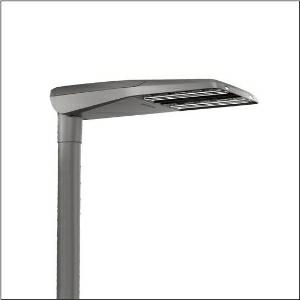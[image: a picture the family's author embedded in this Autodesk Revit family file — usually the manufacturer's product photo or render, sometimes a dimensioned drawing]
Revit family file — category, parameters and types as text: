
# Revit family: streetlight_sl_11_iq_midi___st0_5st0_5_5xc3h51f08me_c4bc
name_source: partatom
category: Lighting Fixtures
units: mm (PartAtom-declared; Revit-internal decimal feet)

## family parameters
Cut with Voids When Loaded = No
Host = Face
Light Source = No
Part Type = Normal
Room Calculation Point = No
Round Connector Dimension = Use Diameter
Shared = No

## types (1)
- --- (1 x LED, 17940 lm, 124.7 W, 3000K)
    Apparent Load = 125 VA
    CIE Flux Codes = 43 74 97 100 100
    Color Rendering = 70
    Color Temperature = 3000K
    Default Elevation = 1800 mm
    Description = Streetlight SL 11 iQ midi, mast luminaire, primary light control with 3 zone facetted reflector, of plastic, silver coated, highly specular, primary optical cover: cover, of PMMA, transparent, light distribution: ST0.5ST0.5, light emission: direct distribution, primary light characteristic: asymmetric, installation type: post-top, side-entry, LED, High Power LED, rated luminous flux: 17.940lm, luminous efficacy: 144lm/W, light colour: 730, colour temperature: 3000K, control: Street-Remote, optimised constant luminous flux control (CLO 2.0), Desk-Remote (wireless, voltage-free reading and setting of iQ features in the workshop via application-optimized NFC function/RFID function), Light-Fading, Smart-Wire, Night-Set, Lumen-Switch, Temp-Guard, Auto-Match, with cable H07RN-F 5x 1.5mm², mains connection: 220..240V, AC, 50/60Hz, connection cable pre-assembled, cable length: 12,5m, start of lifetime: 125W, end of lifetime: 132W, reduction: 57W, luminaire housing, of diecast aluminium, powder-coated, Siteco® metallic grey (DB 702S), length: 780mm, width: 376mm, height: 118mm, spigot size: 60/76mm (post-top) and 42/60/76mm (side-entry), mast flange for spigot size: 42mm: 5XC10008XM4, 60mm: 5XC10008XM2, 76/60mm: 5XC10108XM1, equipment: Power, protection rating (complete): IP66, insulation class (complete): insulation class II (safety insulation), certification: CE, ENEC, VDE, impact resistance: IK09, permissible operating ambient temperature for outdoor applications: -25..+50°C, standard-compliant lighting for roads and squares, packaging unit: 1 piece

Light Distribution: ST0.5ST0.5
    Height = 118 mm
    Lamp = 1 x LED
    Lamp Light Flux = 17940 lm
    Lamp Power = 124.7 W
    Lamp count = 1
    Length = 780 mm
    Luminous efficacy = 144 lm/W
    Manufacturer = Siteco
    ModVariant = No
    Model = 5XC3H51F08ME
    Number of Poles = 1
    OnlyDefault = Yes
    Power Factor = 1
    Product Name = Streetlight SL 11 iQ midi | ST0.5ST0.5
    Product group = mast luminaire | pylon top
    ProductGroupID = 6100
    Protection Class = Protection class II
    Protection Degree = IP 66
    RLX_Detail_Level = 1
    RlxData = <blob elided: 75053 chars, md5=9f03c511>
    Socket = socket
    Standby Power = 0 W
    System Light Flux = 17941 lm
    System Power = 125 W
    Type Comments = factory setting: luminous flux: 100 % | dim-lin: 254 | 557 mA
    Type Image = l_1005960.jpg
    URL = http://relux.com
    VarID = @adj_086437
    Voltage = 0 V
    Weight = 0.00 kg
    Width = 376 mm

## geometry (parser evidence)
native form markers: Blend x4, Sweep x12
no freeform markers — native parametric forms only
